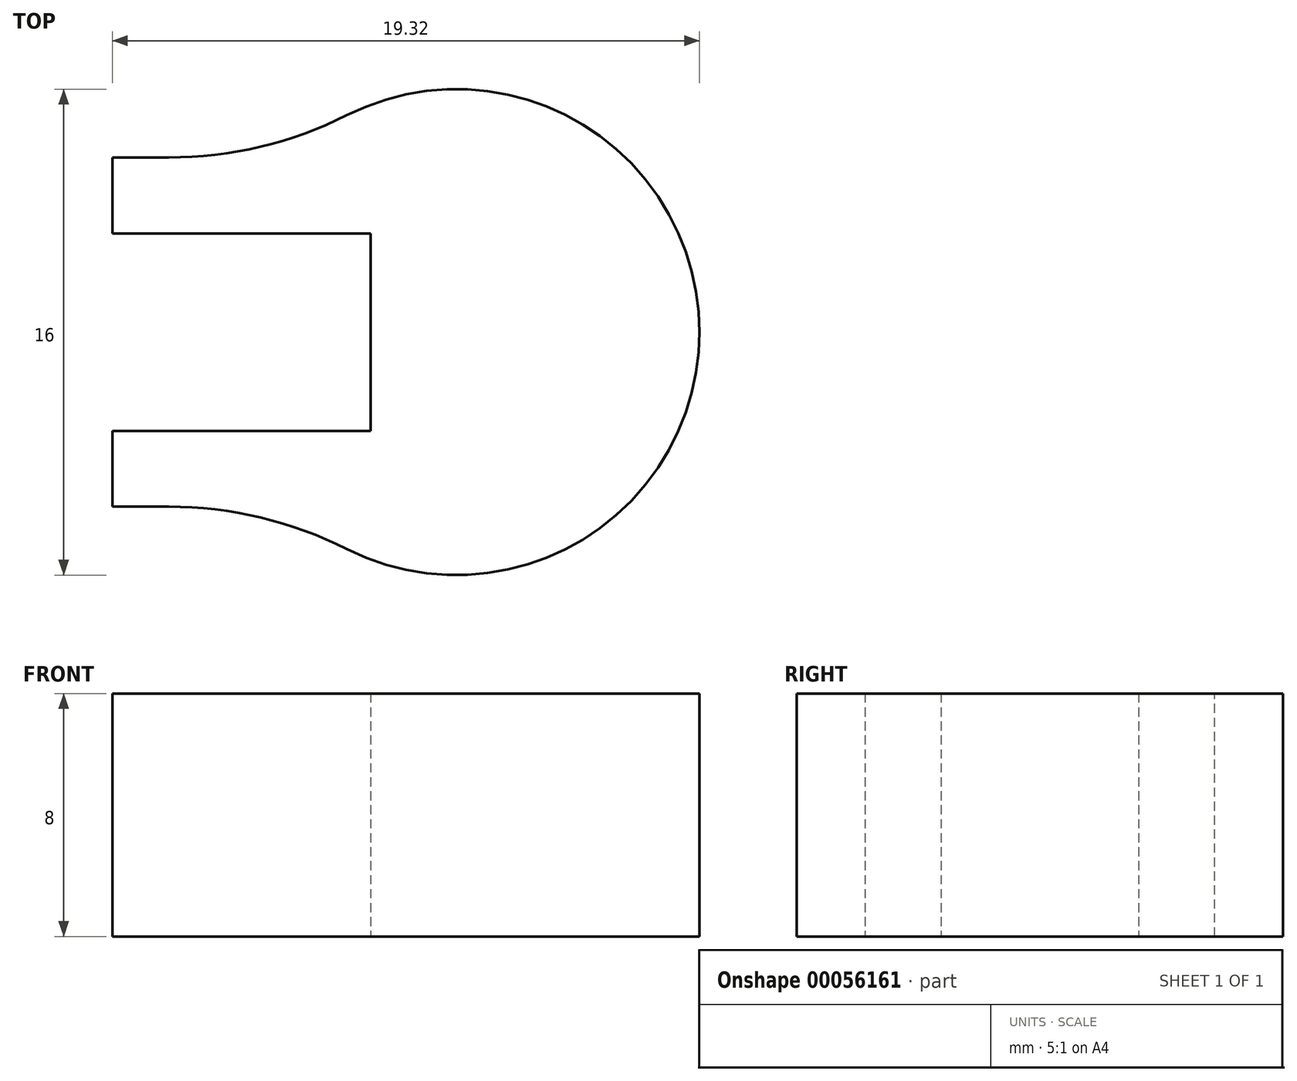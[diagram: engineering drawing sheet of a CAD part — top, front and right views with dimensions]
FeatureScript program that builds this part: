
annotation { "Feature Type Name" : "Feature", "Feature Type Description" : "" }
export const myFeature = defineFeature(function(context is Context, id is Id, definition is map)
    precondition{}
    {
        {
            var Q0;
            Q0=qCreatedBy(makeId("Top.planeOp"),FACE);
            var sketch = newSketch(context, id + "F0", { "sketchPlane" : qUnion([Q0])});
            skLineSegment(sketch, "E0.bottom", {"start": v(-5.24, 0) * mm, "end": v(-11, 0) * mm});
            skLineSegment(sketch, "E0.top", {"start": v(-5.24, 11.5) * mm, "end": v(-11, 11.5) * mm});
            skLineSegment(sketch, "E0.right", {"start": v(-11, 0) * mm, "end": v(-11, 2.5) * mm});
            skLineSegment(sketch, "E1.bottom", {"start": v(-11, 9) * mm, "end": v(-2.5, 9) * mm});
            skLineSegment(sketch, "E1.top", {"start": v(-11, 2.5) * mm, "end": v(-2.5, 2.5) * mm});
            skLineSegment(sketch, "E1.right", {"start": v(-2.5, 9) * mm, "end": v(-2.5, 2.5) * mm});
            skLineSegment(sketch, "E2", {"start": v(0, 5.75) * mm, "end": v(-39.04, 5.75) * mm, "construction": true});
            skLineSegment(sketch, "E3.trimOffspring", {"start": v(-11, 9) * mm, "end": v(-11, 11.5) * mm});
            skPoint(sketch, "E4.orphan", {"position": v(0, 11.5) * mm});
            skPoint(sketch, "E5.orphan", {"position": v(0, 0) * mm});
            skArc(sketch, "E6.trimOffspring", {"start": v(-5.24, 0) * mm, "mid": v(8.32, 5.75) * mm, "end": v(-5.24, 11.5) * mm});
            skSolve(sketch);
        }
        {
            var Q0;
            Q0=makeQuery(id+"F0.imprint","IMPRINT",FACE,{"disambiguationData":[TD([[makeQuery(id+"F0.imprint","IMPRINT",EDGE,{"derivedFrom":sQuery(id+"F0.wireOp",EDGE,"E0.bottom")}),-1.0]])]});
            extrude(context, id + "F1", {"entities" : qUnion([Q0]), "depth" : 8 * mm});
        }
        {
            var Q0;
            Q0=makeQuery(id+"F1.opExtrude","SWEPT_EDGE",EDGE,{"disambiguationData":[OSD([sQuery(id+"F0.wireOp",EDGE,"E0.bottom"),sQuery(id+"F0.wireOp",EDGE,"E6.trimOffspring")])]});
            var Q1;
            Q1=makeQuery(id+"F1.opExtrude","SWEPT_EDGE",EDGE,{"disambiguationData":[OSD([sQuery(id+"F0.wireOp",EDGE,"E0.top"),sQuery(id+"F0.wireOp",EDGE,"E6.trimOffspring")])]});
            fillet(context, id + "F2", {"entities" : qUnion([Q0, Q1]), "radius" : 13 * mm, "tangentPropagation" : true, "allowEdgeOverflow" : false});
        }
    });
